# Revit family: Stand-LAMMHULTS-ADD-Coat
name_source: partatom
category: Furniture
revit_build: Autodesk Revit Architecture 2012 (Build: 20110916_2132(x64)
units: mm (PartAtom-declared; Revit-internal decimal feet)

## types (4) — shared parameters
Assembly Code = E2020
Description = *Please enter mtrl description here for use in mto*
Keynote = 46.B
Legs Material = Colour - Black
Manufacturer = LAMMHULTS
Model = Add Coat
URL = www.lammhults.se

## per-type parameters (varying)
| type | Cloath_Hanger Material | Frame Material | Width | _Width 750 (6 Hooks) |
| Width 75 - Paint/Wood | Wood - Veneer - Ash | Colour - Black | 750 mm  [stored 2.46063 ft] | Yes |
| Width 75 - Chrome | Metal - Chrome - Polished | Metal - Chrome - Polished | 750 mm  [stored 2.46063 ft] | Yes |
| Width 50 - Paint/Wood | Wood - Veneer - Ash | Colour - Black | 500 mm  [stored 1.64042 ft] | No |
| Width 50 - Chrome | Metal - Chrome - Polished | Metal - Chrome - Polished | 500 mm  [stored 1.64042 ft] | No |

note: [stored X ft] marks values corroborated as IEEE doubles in the binary element streams (Revit-internal decimal feet)

## geometry (parser evidence)
native form markers: Blend x4, Sweep x2
no freeform markers — native parametric forms only
